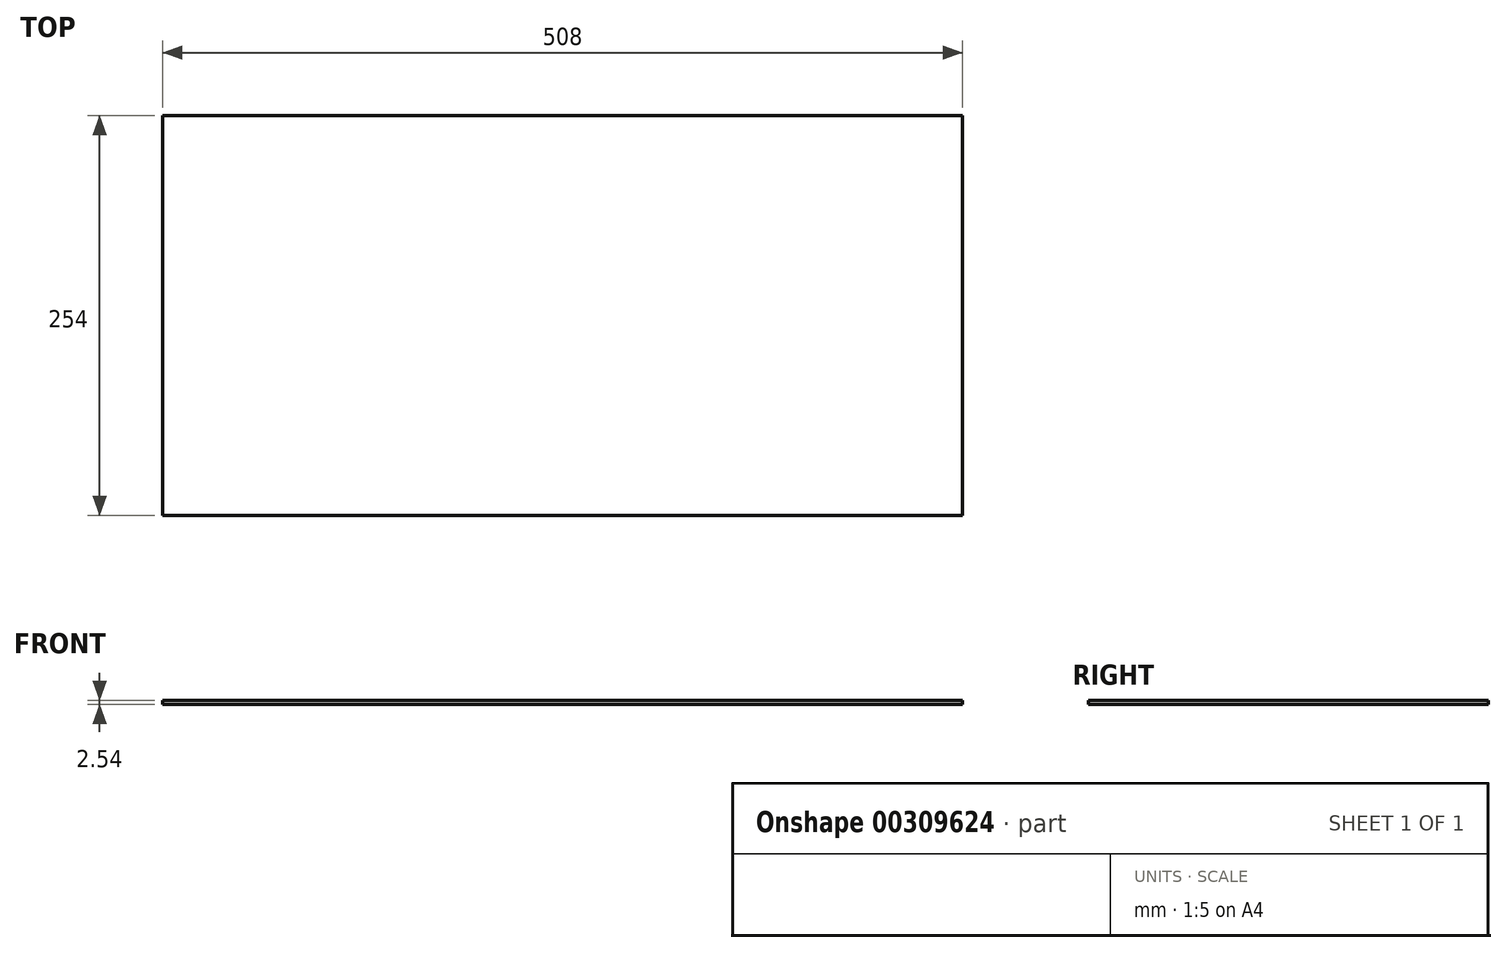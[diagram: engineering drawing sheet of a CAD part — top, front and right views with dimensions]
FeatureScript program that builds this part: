
annotation { "Feature Type Name" : "Feature", "Feature Type Description" : "" }
export const myFeature = defineFeature(function(context is Context, id is Id, definition is map)
    precondition{}
    {
        {
            var Q0;
            Q0=qCreatedBy(makeId("Top.planeOp"),FACE);
            var sketch = newSketch(context, id + "F0", { "sketchPlane" : qUnion([Q0])});
            skLineSegment(sketch, "E0.bottom", {"start": v(-197.29, 124.54) * mm, "end": v(310.71, 124.54) * mm});
            skLineSegment(sketch, "E0.top", {"start": v(-197.29, -129.46) * mm, "end": v(310.71, -129.46) * mm});
            skLineSegment(sketch, "E0.left", {"start": v(-197.29, 124.54) * mm, "end": v(-197.29, -129.46) * mm});
            skLineSegment(sketch, "E0.right", {"start": v(310.71, 124.54) * mm, "end": v(310.71, -129.46) * mm});
            skSolve(sketch);
        }
        {
            var Q0;
            Q0=makeQuery(id+"F0.imprint","IMPRINT",FACE,{"disambiguationData":[TD([[makeQuery(id+"F0.imprint","IMPRINT",EDGE,{"derivedFrom":sQuery(id+"F0.wireOp",EDGE,"E0.bottom")}),-1.0]])]});
            extrude(context, id + "F1", {"entities" : qUnion([Q0]), "depth" : 2.54 * mm});
        }
    });
